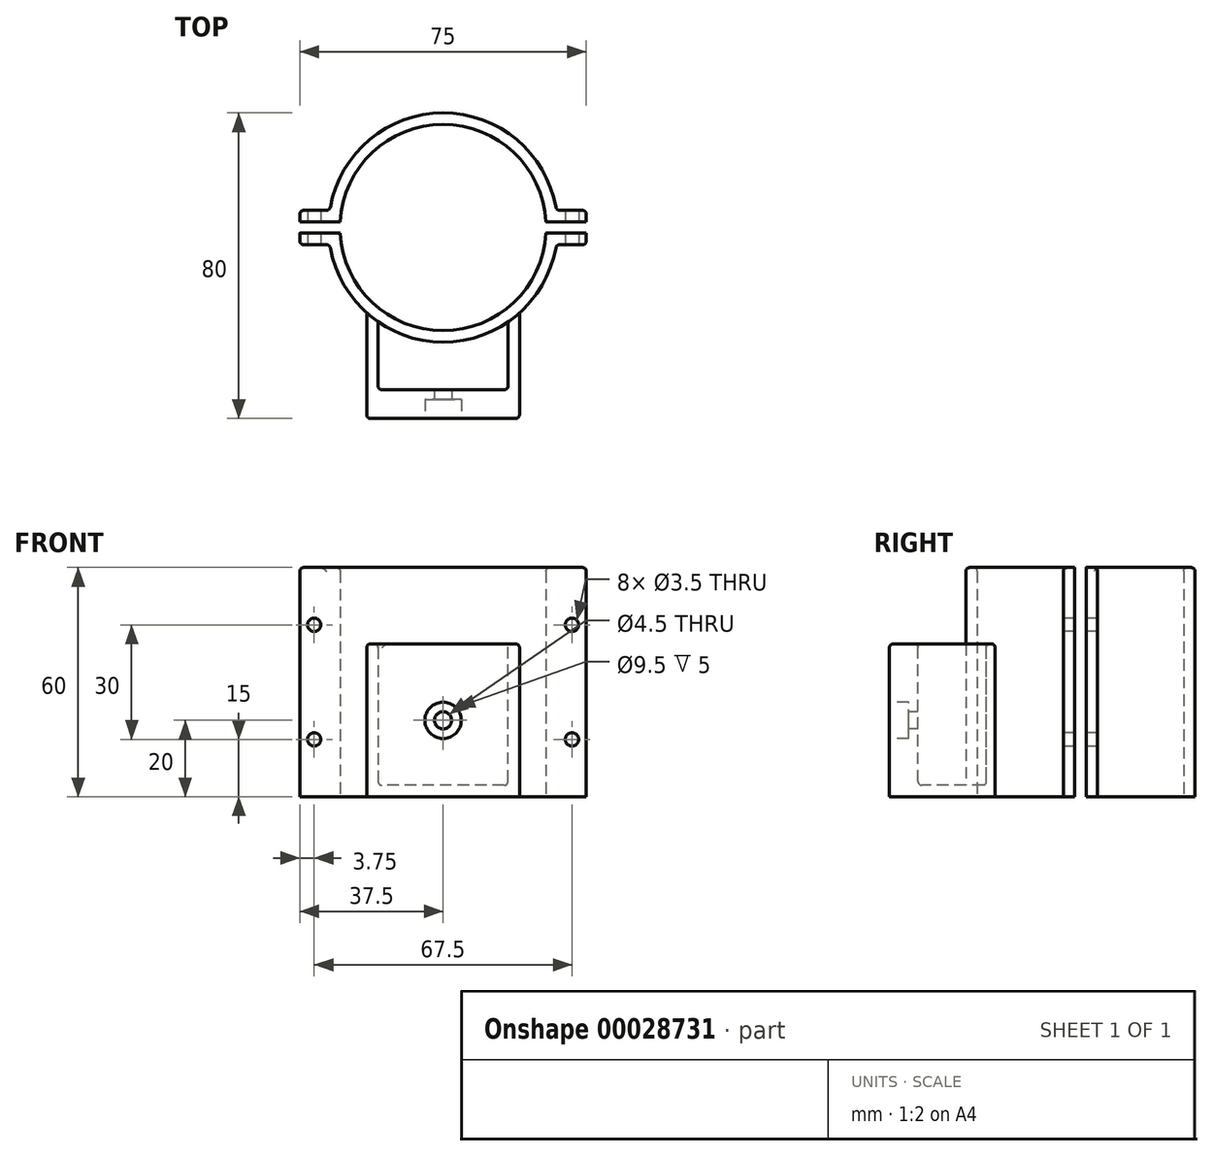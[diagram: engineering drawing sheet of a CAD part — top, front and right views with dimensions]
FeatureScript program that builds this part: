
annotation { "Feature Type Name" : "Feature", "Feature Type Description" : "" }
export const myFeature = defineFeature(function(context is Context, id is Id, definition is map)
    precondition{}
    {
        {
            var Q0;
            Q0=qCreatedBy(makeId("Top.planeOp"),FACE);
            var sketch = newSketch(context, id + "F0", { "sketchPlane" : qUnion([Q0])});
            skArc(sketch, "E0", {"start": v(-26.96, -1.5) * mm, "mid": v(0, -27) * mm, "end": v(26.96, -1.5) * mm});
            skArc(sketch, "E1", {"start": v(-29.66, -4.5) * mm, "mid": v(0, -30) * mm, "end": v(29.66, -4.5) * mm});
            skLineSegment(sketch, "E2.bottom", {"start": v(-37.5, 1.5) * mm, "end": v(-26.96, 1.5) * mm});
            skLineSegment(sketch, "E2.top", {"start": v(-37.5, -1.5) * mm, "end": v(-26.96, -1.5) * mm});
            skLineSegment(sketch, "E3", {"start": v(0, 0) * mm, "end": v(60.03, 0) * mm, "construction": true});
            skLineSegment(sketch, "E4", {"start": v(0, 0) * mm, "end": v(0, 62.27) * mm, "construction": true});
            skLineSegment(sketch, "E5.bottom", {"start": v(-37.5, 1.5) * mm, "end": v(-29.66, 1.5) * mm});
            skLineSegment(sketch, "E5.top", {"start": v(-37.5, 4.5) * mm, "end": v(-29.66, 4.5) * mm});
            skLineSegment(sketch, "E5.left", {"start": v(-37.5, 1.5) * mm, "end": v(-37.5, 4.5) * mm});
            skLineSegment(sketch, "E6.bottom", {"start": v(-37.5, -1.5) * mm, "end": v(-29.66, -1.5) * mm});
            skLineSegment(sketch, "E6.top", {"start": v(-37.5, -4.5) * mm, "end": v(-29.66, -4.5) * mm});
            skLineSegment(sketch, "E6.left", {"start": v(-37.5, -1.5) * mm, "end": v(-37.5, -4.5) * mm});
            skLineSegment(sketch, "E7.bottom", {"start": v(37.5, 1.5) * mm, "end": v(29.66, 1.5) * mm});
            skLineSegment(sketch, "E7.top", {"start": v(37.5, 4.5) * mm, "end": v(29.66, 4.5) * mm});
            skLineSegment(sketch, "E7.left", {"start": v(37.5, 1.5) * mm, "end": v(37.5, 4.5) * mm});
            skLineSegment(sketch, "E8.bottom", {"start": v(37.5, -1.5) * mm, "end": v(29.66, -1.5) * mm});
            skLineSegment(sketch, "E8.top", {"start": v(37.5, -4.5) * mm, "end": v(29.66, -4.5) * mm});
            skLineSegment(sketch, "E8.left", {"start": v(37.5, -1.5) * mm, "end": v(37.5, -4.5) * mm});
            skLineSegment(sketch, "E9.trimOffspring", {"start": v(26.96, 1.5) * mm, "end": v(37.5, 1.5) * mm});
            skLineSegment(sketch, "E10.trimOffspring", {"start": v(26.96, -1.5) * mm, "end": v(37.5, -1.5) * mm});
            skArc(sketch, "E11.trimOffspring", {"start": v(26.96, 1.5) * mm, "mid": v(0, 27) * mm, "end": v(-26.96, 1.5) * mm});
            skArc(sketch, "E12.trimOffspring", {"start": v(29.66, 4.5) * mm, "mid": v(0, 30) * mm, "end": v(-29.66, 4.5) * mm});
            skSolve(sketch);
        }
        {
            var Q0;
            Q0 = qSketchRegion(id + "F0", true);
            extrude(context, id + "F1", {"entities" : qUnion([Q0]), "depth" : 60 * mm});
        }
        {
            var Q0;
            Q0=qCreatedBy(makeId("Front.planeOp"),FACE);
            cPlane(context, id + "F2", {"entities" : qUnion([Q0]), "cplaneType" : CPlaneType.OFFSET, "offset" : 50 * mm, "width" : 150 * mm, "height" : 150 * mm});
        }
        {
            var Q0;
            Q0=qCreatedBy(id+"F2.planeOp",FACE);
            var sketch = newSketch(context, id + "F3", { "sketchPlane" : qUnion([Q0])});
            skLineSegment(sketch, "E13.bottom", {"start": v(-20, 40) * mm, "end": v(-17, 40) * mm});
            skLineSegment(sketch, "E13.top", {"start": v(-20, 0) * mm, "end": v(20, 0) * mm});
            skLineSegment(sketch, "E13.left", {"start": v(-20, 40) * mm, "end": v(-20, 0) * mm});
            skLineSegment(sketch, "E13.right", {"start": v(20, 40) * mm, "end": v(20, 0) * mm});
            skLineSegment(sketch, "E14", {"start": v(0, 0) * mm, "end": v(0, 107.1) * mm, "construction": true});
            skLineSegment(sketch, "E15", {"start": v(0, 0) * mm, "end": v(80.36, 0) * mm, "construction": true});
            skLineSegment(sketch, "E16.top", {"start": v(-17, 3) * mm, "end": v(17, 3) * mm});
            skLineSegment(sketch, "E16.left", {"start": v(-17, 40) * mm, "end": v(-17, 3) * mm});
            skLineSegment(sketch, "E16.right", {"start": v(17, 40) * mm, "end": v(17, 3) * mm});
            skLineSegment(sketch, "E17.trimOffspring", {"start": v(17, 40) * mm, "end": v(20, 40) * mm});
            skSolve(sketch);
        }
        {
            var Q0;
            Q0 = qSketchRegion(id + "F3", true);
            var Q1;
            Q1=makeQuery(id+"F1.opExtrude","SWEPT_BODY",BODY,{"disambiguationData":[OSD([sQuery(id+"F0.wireOp",EDGE,"E0"),sQuery(id+"F0.wireOp",EDGE,"E1")])]});
            extrude(context, id + "F4", {"entities" : qUnion([Q0]), "operationType" : NewBodyOperationType.ADD, "endBound" : BoundingType.UP_TO_NEXT, "oppositeDirection" : true, "endBoundEntityBody" : qUnion([Q1]), "depth" : 25 * mm});
        }
        {
            var Q0;
            Q0=qCreatedBy(id+"F2.planeOp",FACE);
            var sketch = newSketch(context, id + "F5", { "sketchPlane" : qUnion([Q0])});
            skLineSegment(sketch, "E18.bottom", {"start": v(-20, 0) * mm, "end": v(20, 0) * mm});
            skLineSegment(sketch, "E18.top", {"start": v(-20, 40) * mm, "end": v(20, 40) * mm});
            skLineSegment(sketch, "E18.left", {"start": v(-20, 0) * mm, "end": v(-20, 40) * mm});
            skLineSegment(sketch, "E18.right", {"start": v(20, 0) * mm, "end": v(20, 40) * mm});
            skSolve(sketch);
        }
        {
            var Q0;
            Q0 = qSketchRegion(id + "F5", true);
            extrude(context, id + "F6", {"entities" : qUnion([Q0]), "operationType" : NewBodyOperationType.ADD, "oppositeDirection" : true, "depth" : 7.5 * mm});
        }
        {
            var Q0;
            Q0=makeQuery(id+"F4.opExtrude","CAP_EDGE",EDGE,{"disambiguationData":[OSD([sQuery(id+"F3.wireOp",EDGE,"E13.right")])],"isStart":false});
            var Q1;
            Q1=makeQuery(id+"F4.opExtrude","CAP_EDGE",EDGE,{"disambiguationData":[OSD([sQuery(id+"F3.wireOp",EDGE,"E17.trimOffspring")])],"isStart":false});
            var Q2;
            Q2=makeQuery(id+"F4.opExtrude","CAP_EDGE",EDGE,{"disambiguationData":[OSD([sQuery(id+"F3.wireOp",EDGE,"E16.left")])],"isStart":false});
            var Q3;
            Q3=makeQuery(id+"F4.opExtrude","CAP_EDGE",EDGE,{"disambiguationData":[OSD([sQuery(id+"F3.wireOp",EDGE,"E13.bottom")])],"isStart":false});
            var Q4;
            Q4=makeQuery(id+"F4.opExtrude","CAP_EDGE",EDGE,{"disambiguationData":[OSD([sQuery(id+"F3.wireOp",EDGE,"E13.left")])],"isStart":false});
            var Q5;
            Q5=makeQuery(id+"F4.opExtrude","CAP_EDGE",EDGE,{"disambiguationData":[OSD([sQuery(id+"F3.wireOp",EDGE,"E16.right")])],"isStart":false});
            var Q6;
            Q6=makeQuery(id+"F4.opExtrude","CAP_EDGE",EDGE,{"disambiguationData":[OSD([sQuery(id+"F3.wireOp",EDGE,"E16.top")])],"isStart":false});
            var Q7;
            Q7=makeQuery(id+"F4.opExtrude","SWEPT_EDGE",EDGE,{"disambiguationData":[OSD([sQuery(id+"F3.wireOp",EDGE,"E16.top"),sQuery(id+"F3.wireOp",EDGE,"E16.right")])]});
            var Q8;
            Q8=makeQuery(id+"F6.boolean.opBoolean","INTERSECT",EDGE,{"derivedFrom":[makeQuery(id+"F4.opExtrude","SWEPT_FACE",FACE,{"disambiguationData":[OSD([sQuery(id+"F3.wireOp",EDGE,"E16.right")])]}),makeQuery(id+"F6.opExtrude","CAP_FACE",FACE,{"disambiguationData":[OSD([sQuery(id+"F5.wireOp",EDGE,"E18.bottom"),sQuery(id+"F5.wireOp",EDGE,"E18.top"),sQuery(id+"F5.wireOp",EDGE,"E18.left"),sQuery(id+"F5.wireOp",EDGE,"E18.right")])],"isStart":false})]});
            var Q9;
            Q9=makeQuery(id+"F6.boolean.opBoolean","INTERSECT",EDGE,{"derivedFrom":[makeQuery(id+"F4.opExtrude","SWEPT_FACE",FACE,{"disambiguationData":[OSD([sQuery(id+"F3.wireOp",EDGE,"E16.top")])]}),makeQuery(id+"F6.opExtrude","CAP_FACE",FACE,{"disambiguationData":[OSD([sQuery(id+"F5.wireOp",EDGE,"E18.bottom"),sQuery(id+"F5.wireOp",EDGE,"E18.top"),sQuery(id+"F5.wireOp",EDGE,"E18.left"),sQuery(id+"F5.wireOp",EDGE,"E18.right")])],"isStart":false})]});
            var Q10;
            Q10=makeQuery(id+"F4.opExtrude","SWEPT_EDGE",EDGE,{"disambiguationData":[OSD([sQuery(id+"F3.wireOp",EDGE,"E16.top"),sQuery(id+"F3.wireOp",EDGE,"E16.left")])]});
            var Q11;
            Q11=makeQuery(id+"F6.boolean.opBoolean","INTERSECT",EDGE,{"derivedFrom":[makeQuery(id+"F4.opExtrude","SWEPT_FACE",FACE,{"disambiguationData":[OSD([sQuery(id+"F3.wireOp",EDGE,"E16.left")])]}),makeQuery(id+"F6.opExtrude","CAP_FACE",FACE,{"disambiguationData":[OSD([sQuery(id+"F5.wireOp",EDGE,"E18.bottom"),sQuery(id+"F5.wireOp",EDGE,"E18.top"),sQuery(id+"F5.wireOp",EDGE,"E18.left"),sQuery(id+"F5.wireOp",EDGE,"E18.right")])],"isStart":false})]});
            var Q12;
            Q12=makeQuery(id+"F4.opExtrude","SWEPT_EDGE",EDGE,{"disambiguationData":[OSD([sQuery(id+"F3.wireOp",EDGE,"E13.bottom"),sQuery(id+"F3.wireOp",EDGE,"E13.left")])]});
            var Q13;
            Q13=makeQuery(id+"F4.opExtrude","SWEPT_EDGE",EDGE,{"disambiguationData":[OSD([sQuery(id+"F3.wireOp",EDGE,"E13.bottom"),sQuery(id+"F3.wireOp",EDGE,"E16.left")])]});
            var Q14;
            Q14=makeQuery(id+"F4.opExtrude","SWEPT_EDGE",EDGE,{"disambiguationData":[OSD([sQuery(id+"F3.wireOp",EDGE,"E13.right"),sQuery(id+"F3.wireOp",EDGE,"E17.trimOffspring")])]});
            var Q15;
            Q15=makeQuery(id+"F4.opExtrude","CAP_EDGE",EDGE,{"disambiguationData":[OSD([sQuery(id+"F3.wireOp",EDGE,"E13.left")])],"isStart":true});
            var Q16;
            Q16=makeQuery(id+"F4.opExtrude","CAP_EDGE",EDGE,{"disambiguationData":[OSD([sQuery(id+"F3.wireOp",EDGE,"E13.right")])],"isStart":true});
            var Q17;
            Q17=makeQuery(id+"F6.boolean.opBoolean","MERGE",EDGE,{"derivedFrom":[makeQuery(id+"F4.opExtrude","CAP_EDGE",EDGE,{"disambiguationData":[OSD([sQuery(id+"F3.wireOp",EDGE,"E13.bottom")])],"isStart":true}),makeQuery(id+"F4.opExtrude","CAP_EDGE",EDGE,{"disambiguationData":[OSD([sQuery(id+"F3.wireOp",EDGE,"E17.trimOffspring")])],"isStart":true}),makeQuery(id+"F6.opExtrude","CAP_EDGE",EDGE,{"disambiguationData":[OSD([sQuery(id+"F5.wireOp",EDGE,"E18.top")])],"isStart":true})]});
            var Q18;
            Q18=makeQuery(id+"F1.opExtrude","CAP_EDGE",EDGE,{"disambiguationData":[OSD([sQuery(id+"F0.wireOp",EDGE,"E1")])],"isStart":false});
            var Q19;
            Q19=makeQuery(id+"F1.opExtrude","CAP_EDGE",EDGE,{"disambiguationData":[OSD([sQuery(id+"F0.wireOp",EDGE,"E0")])],"isStart":false});
            var Q20;
            Q20=makeQuery(id+"F1.opExtrude","SWEPT_EDGE",EDGE,{"disambiguationData":[OSD([sQuery(id+"F0.wireOp",EDGE,"E1"),sQuery(id+"F0.wireOp",EDGE,"E8.top")])]});
            var Q21;
            Q21=makeQuery(id+"F1.opExtrude","CAP_EDGE",EDGE,{"disambiguationData":[OSD([sQuery(id+"F0.wireOp",EDGE,"E8.top")])],"isStart":false});
            var Q22;
            Q22=makeQuery(id+"F1.opExtrude","SWEPT_EDGE",EDGE,{"disambiguationData":[OSD([sQuery(id+"F0.wireOp",EDGE,"E8.top"),sQuery(id+"F0.wireOp",EDGE,"E8.left")])]});
            var Q23;
            Q23=makeQuery(id+"F1.opExtrude","CAP_EDGE",EDGE,{"disambiguationData":[OSD([sQuery(id+"F0.wireOp",EDGE,"E8.left")])],"isStart":false});
            var Q24;
            Q24=makeQuery(id+"F1.opExtrude","CAP_EDGE",EDGE,{"disambiguationData":[OSD([sQuery(id+"F0.wireOp",EDGE,"E7.left")])],"isStart":false});
            var Q25;
            Q25=makeQuery(id+"F1.opExtrude","SWEPT_EDGE",EDGE,{"disambiguationData":[OSD([sQuery(id+"F0.wireOp",EDGE,"E7.top"),sQuery(id+"F0.wireOp",EDGE,"E7.left")])]});
            var Q26;
            Q26=makeQuery(id+"F1.opExtrude","CAP_EDGE",EDGE,{"disambiguationData":[OSD([sQuery(id+"F0.wireOp",EDGE,"E12.trimOffspring")])],"isStart":false});
            var Q27;
            Q27=makeQuery(id+"F1.opExtrude","CAP_EDGE",EDGE,{"disambiguationData":[OSD([sQuery(id+"F0.wireOp",EDGE,"E7.top")])],"isStart":false});
            var Q28;
            Q28=makeQuery(id+"F1.opExtrude","SWEPT_EDGE",EDGE,{"disambiguationData":[OSD([sQuery(id+"F0.wireOp",EDGE,"E7.top"),sQuery(id+"F0.wireOp",EDGE,"E12.trimOffspring")])]});
            var Q29;
            Q29=makeQuery(id+"F1.opExtrude","SWEPT_EDGE",EDGE,{"disambiguationData":[OSD([sQuery(id+"F0.wireOp",EDGE,"E5.top"),sQuery(id+"F0.wireOp",EDGE,"E12.trimOffspring")])]});
            var Q30;
            Q30=makeQuery(id+"F1.opExtrude","SWEPT_EDGE",EDGE,{"disambiguationData":[OSD([sQuery(id+"F0.wireOp",EDGE,"E5.top"),sQuery(id+"F0.wireOp",EDGE,"E5.left")])]});
            var Q31;
            Q31=makeQuery(id+"F1.opExtrude","CAP_EDGE",EDGE,{"disambiguationData":[OSD([sQuery(id+"F0.wireOp",EDGE,"E5.left")])],"isStart":false});
            var Q32;
            Q32=makeQuery(id+"F1.opExtrude","CAP_EDGE",EDGE,{"disambiguationData":[OSD([sQuery(id+"F0.wireOp",EDGE,"E6.top")])],"isStart":false});
            var Q33;
            Q33=makeQuery(id+"F1.opExtrude","SWEPT_EDGE",EDGE,{"disambiguationData":[OSD([sQuery(id+"F0.wireOp",EDGE,"E6.top"),sQuery(id+"F0.wireOp",EDGE,"E6.left")])]});
            var Q34;
            Q34=makeQuery(id+"F1.opExtrude","SWEPT_EDGE",EDGE,{"disambiguationData":[OSD([sQuery(id+"F0.wireOp",EDGE,"E1"),sQuery(id+"F0.wireOp",EDGE,"E6.top")])]});
            var Q35;
            Q35=makeQuery(id+"F1.opExtrude","CAP_EDGE",EDGE,{"disambiguationData":[OSD([sQuery(id+"F0.wireOp",EDGE,"E6.left")])],"isStart":false});
            var Q36;
            Q36=makeQuery(id+"F1.opExtrude","CAP_EDGE",EDGE,{"disambiguationData":[OSD([sQuery(id+"F0.wireOp",EDGE,"E11.trimOffspring")])],"isStart":false});
            fillet(context, id + "F7", {"entities" : qUnion([Q0, Q1, Q2, Q3, Q4, Q5, Q6, Q7, Q8, Q9, Q10, Q11, Q12, Q13, Q14, Q15, Q16, Q17, Q18, Q19, Q20, Q21, Q22, Q23, Q24, Q25, Q26, Q27, Q28, Q29, Q30, Q31, Q32, Q33, Q34, Q35, Q36]), "radius" : 1 * mm, "tangentPropagation" : true, "allowEdgeOverflow" : false});
        }
        {
            var Q0;
            Q0=qCreatedBy(id+"F2.planeOp",FACE);
            var sketch = newSketch(context, id + "F8", { "sketchPlane" : qUnion([Q0])});
            skCircle(sketch, "E19", {"center": v(0, 20) * mm, "radius": 2.25 * mm});
            skSolve(sketch);
        }
        {
            var Q0;
            Q0 = qSketchRegion(id + "F8", true);
            extrude(context, id + "F9", {"entities" : qUnion([Q0]), "operationType" : NewBodyOperationType.REMOVE, "oppositeDirection" : true, "depth" : 10 * mm});
        }
        {
            var Q0;
            Q0=qCreatedBy(id+"F2.planeOp",FACE);
            var sketch = newSketch(context, id + "F10", { "sketchPlane" : qUnion([Q0])});
            skCircle(sketch, "E20", {"center": v(0, 20) * mm, "radius": 4.75 * mm});
            skSolve(sketch);
        }
        {
            var Q0;
            Q0 = qSketchRegion(id + "F10", true);
            extrude(context, id + "F11", {"entities" : qUnion([Q0]), "operationType" : NewBodyOperationType.REMOVE, "oppositeDirection" : true, "depth" : 5 * mm});
        }
        {
            var Q0;
            Q0=qCreatedBy(makeId("Front.planeOp"),FACE);
            var sketch = newSketch(context, id + "F12", { "sketchPlane" : qUnion([Q0])});
            skLineSegment(sketch, "E21", {"start": v(0, 0) * mm, "end": v(0, 74.17) * mm, "construction": true});
            skLineSegment(sketch, "E22", {"start": v(-33.75, -8.97) * mm, "end": v(-33.75, 73.16) * mm, "construction": true});
            skLineSegment(sketch, "E23", {"start": v(33.75, -7.2) * mm, "end": v(33.75, 71.9) * mm, "construction": true});
            skLineSegment(sketch, "E24", {"start": v(-55.85, 15) * mm, "end": v(57.87, 15) * mm, "construction": true});
            skLineSegment(sketch, "E25", {"start": v(-57.87, 45) * mm, "end": v(57.11, 45) * mm, "construction": true});
            skCircle(sketch, "E26", {"center": v(-33.75, 45) * mm, "radius": 1.75 * mm});
            skCircle(sketch, "E27", {"center": v(-33.75, 15) * mm, "radius": 1.75 * mm});
            skCircle(sketch, "E28", {"center": v(33.75, 45) * mm, "radius": 1.75 * mm});
            skCircle(sketch, "E29", {"center": v(33.75, 15) * mm, "radius": 1.75 * mm});
            skSolve(sketch);
        }
        {
            var Q0;
            Q0 = qSketchRegion(id + "F12", true);
            extrude(context, id + "F13", {"entities" : qUnion([Q0]), "operationType" : NewBodyOperationType.REMOVE, "endBound" : BoundingType.SYMMETRIC, "oppositeDirection" : true, "depth" : 25 * mm});
        }
    });
